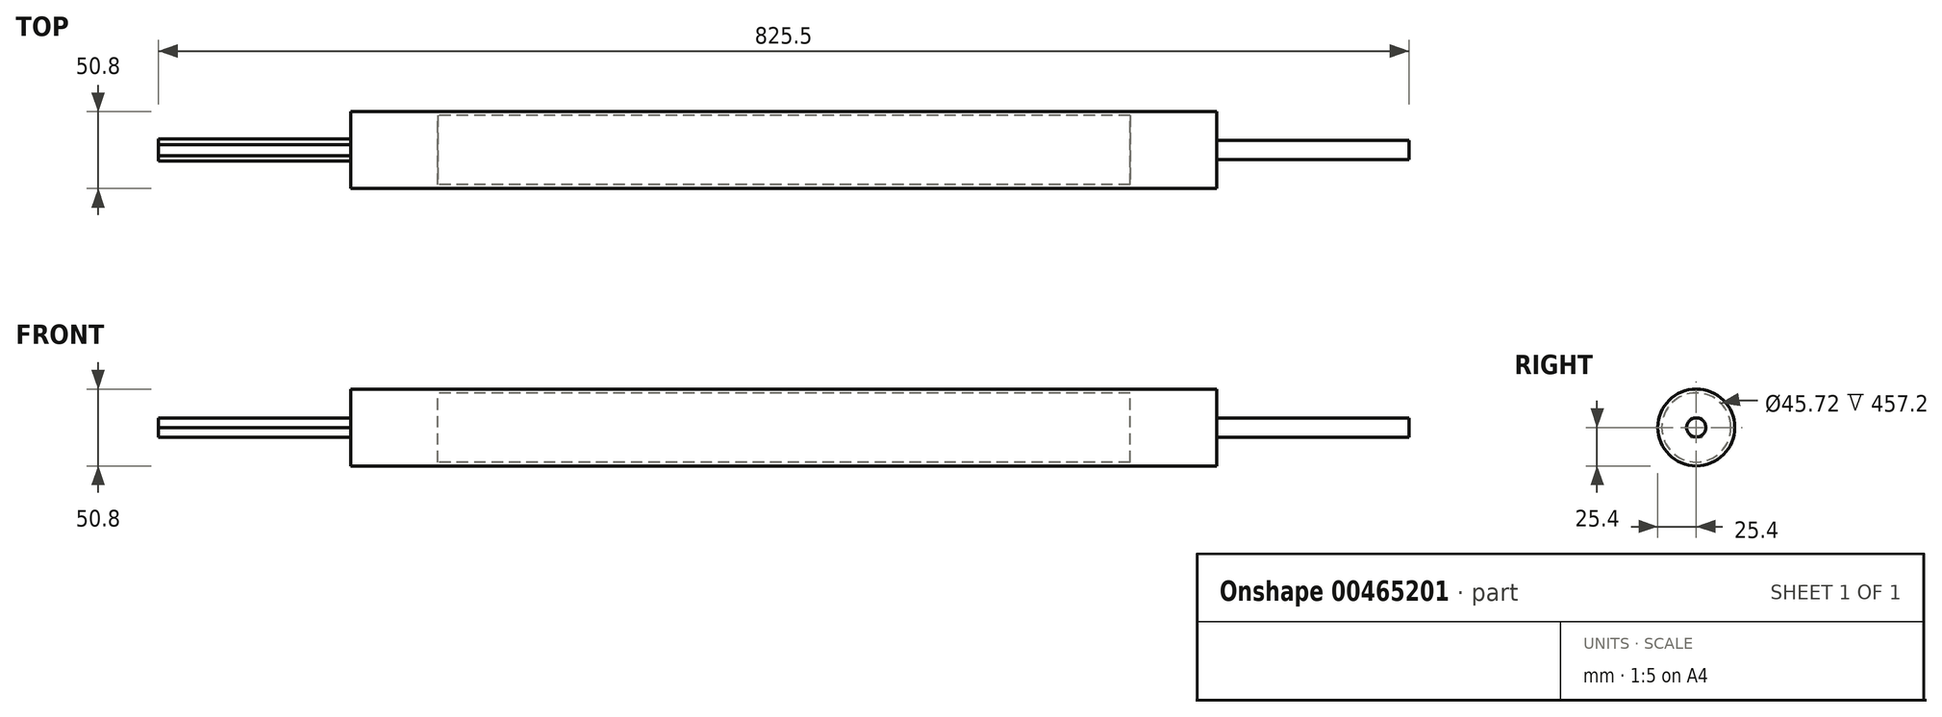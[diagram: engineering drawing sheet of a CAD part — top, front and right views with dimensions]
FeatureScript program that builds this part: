
annotation { "Feature Type Name" : "Feature", "Feature Type Description" : "" }
export const myFeature = defineFeature(function(context is Context, id is Id, definition is map)
    precondition{}
    {
        {
            var Q0;
            Q0=qCreatedBy(makeId("Right.planeOp"),FACE);
            var sketch = newSketch(context, id + "F0", { "sketchPlane" : qUnion([Q0])});
            skCircle(sketch, "E0", {"center": v(0, 0) * mm, "radius": 25.4 * mm});
            skCircle(sketch, "E1", {"center": v(0, 0) * mm, "radius": 22.86 * mm});
            skSolve(sketch);
        }
        {
            var Q0;
            Q0=makeQuery(id+"F0.imprint","IMPRINT",FACE,{"disambiguationData":[TD([[makeQuery(id+"F0.imprint","IMPRINT",EDGE,{"derivedFrom":sQuery(id+"F0.wireOp",EDGE,"E0")}),1.0]])]});
            extrude(context, id + "F1", {"entities" : qUnion([Q0]), "depth" : 558.8 * mm});
        }
        {
            var Q0;
            Q0=makeQuery(id+"F1.opExtrude","CAP_FACE",FACE,{"disambiguationData":[OSD([sQuery(id+"F0.wireOp",EDGE,"E0"),sQuery(id+"F0.wireOp",EDGE,"E1")])],"isStart":false});
            var sketch = newSketch(context, id + "F2", { "sketchPlane" : qUnion([Q0])});
            skCircle(sketch, "E2.0", {"center": v(0, 0) * mm, "radius": 22.86 * mm});
            skCircle(sketch, "E3", {"center": v(0, 0) * mm, "radius": 25.4 * mm});
            skCircle(sketch, "E4", {"center": v(0, 0) * mm, "radius": 6.35 * mm});
            skSolve(sketch);
        }
        {
            var Q0;
            Q0=makeQuery(id+"F2.imprint","IMPRINT",FACE,{"disambiguationData":[TD([[makeQuery(id+"F2.imprint","IMPRINT",EDGE,{"derivedFrom":sQuery(id+"F2.wireOp",EDGE,"E2.0")}),1.0]])]});
            var Q1;
            Q1=makeQuery(id+"F2.imprint","IMPRINT",FACE,{"disambiguationData":[TD([[makeQuery(id+"F2.imprint","IMPRINT",EDGE,{"derivedFrom":sQuery(id+"F2.wireOp",EDGE,"E4")}),1.0]])]});
            extrude(context, id + "F3", {"entities" : qUnion([Q0, Q1]), "oppositeDirection" : true, "depth" : 50.8 * mm});
        }
        {
            var Q0;
            Q0=makeQuery(id+"F2.imprint","IMPRINT",FACE,{"disambiguationData":[TD([[makeQuery(id+"F2.imprint","IMPRINT",EDGE,{"derivedFrom":sQuery(id+"F2.wireOp",EDGE,"E4")}),1.0]])]});
            extrude(context, id + "F4", {"entities" : qUnion([Q0]), "operationType" : NewBodyOperationType.ADD, "depth" : 133.35 * mm});
        }
        {
            var Q0;
            Q0=makeQuery(id+"F2.imprint","IMPRINT",FACE,{"disambiguationData":[TD([[makeQuery(id+"F2.imprint","IMPRINT",EDGE,{"derivedFrom":sQuery(id+"F2.wireOp",EDGE,"E2.0")}),1.0]])]});
            var Q1;
            Q1=makeQuery(id+"F2.imprint","IMPRINT",FACE,{"disambiguationData":[TD([[makeQuery(id+"F2.imprint","IMPRINT",EDGE,{"derivedFrom":sQuery(id+"F2.wireOp",EDGE,"E2.0")}),-1.0]])]});
            var Q2;
            Q2=makeQuery(id+"F2.imprint","IMPRINT",FACE,{"disambiguationData":[TD([[makeQuery(id+"F2.imprint","IMPRINT",EDGE,{"derivedFrom":sQuery(id+"F2.wireOp",EDGE,"E3")}),1.0]])]});
            var Q3;
            Q3=makeQuery(id+"F2.imprint","IMPRINT",FACE,{"disambiguationData":[TD([[makeQuery(id+"F2.imprint","IMPRINT",EDGE,{"derivedFrom":sQuery(id+"F2.wireOp",EDGE,"E4")}),1.0]])]});
            extrude(context, id + "F5", {"entities" : qUnion([Q0, Q1, Q2, Q3]), "operationType" : NewBodyOperationType.ADD, "depth" : 6.35 * mm});
        }
        {
            var Q0;
            Q0=makeQuery(id+"F1.opExtrude","CAP_FACE",FACE,{"disambiguationData":[OSD([sQuery(id+"F0.wireOp",EDGE,"E0"),sQuery(id+"F0.wireOp",EDGE,"E1")])],"isStart":true});
            var sketch = newSketch(context, id + "F6", { "sketchPlane" : qUnion([Q0])});
            skCircle(sketch, "E5", {"center": v(0, 0) * mm, "radius": 25.4 * mm});
            skCircle(sketch, "E6.0", {"center": v(0, 0) * mm, "radius": 22.86 * mm});
            skCircle(sketch, "E7.cCircle", {"center": v(0, 0) * mm, "radius": 6.35 * mm, "construction": true});
            skLineSegment(sketch, "E7.0", {"start": v(3.67, -6.35) * mm, "end": v(-3.67, -6.35) * mm});
            skLineSegment(sketch, "E7.1", {"start": v(-3.67, -6.35) * mm, "end": v(-7.33, 0) * mm});
            skLineSegment(sketch, "E7.2", {"start": v(-7.33, 0) * mm, "end": v(-3.67, 6.35) * mm});
            skLineSegment(sketch, "E7.3", {"start": v(-3.67, 6.35) * mm, "end": v(3.67, 6.35) * mm});
            skLineSegment(sketch, "E7.4", {"start": v(3.67, 6.35) * mm, "end": v(7.33, 0) * mm});
            skLineSegment(sketch, "E7.5", {"start": v(7.33, 0) * mm, "end": v(3.67, -6.35) * mm});
            skPoint(sketch, "E7.0.midPoint", {"position": v(0, -6.35) * mm});
            skSolve(sketch);
        }
        {
            var Q0;
            Q0=makeQuery(id+"F6.imprint","IMPRINT",FACE,{"disambiguationData":[TD([[makeQuery(id+"F6.imprint","IMPRINT",EDGE,{"derivedFrom":sQuery(id+"F6.wireOp",EDGE,"E6.0")}),-1.0]])]});
            var Q1;
            Q1=makeQuery(id+"F6.imprint","IMPRINT",FACE,{"disambiguationData":[TD([[makeQuery(id+"F6.imprint","IMPRINT",EDGE,{"derivedFrom":sQuery(id+"F6.wireOp",EDGE,"E7.0")}),-1.0]])]});
            extrude(context, id + "F7", {"entities" : qUnion([Q0, Q1]), "oppositeDirection" : true, "depth" : 50.8 * mm});
        }
        {
            var Q0;
            Q0=makeQuery(id+"F6.imprint","IMPRINT",FACE,{"disambiguationData":[TD([[makeQuery(id+"F6.imprint","IMPRINT",EDGE,{"derivedFrom":sQuery(id+"F6.wireOp",EDGE,"E7.0")}),-1.0]])]});
            extrude(context, id + "F8", {"entities" : qUnion([Q0]), "operationType" : NewBodyOperationType.ADD, "depth" : 133.35 * mm});
        }
        {
            var Q0;
            Q0 = qSketchRegion(id + "F6", true);
            var Q1;
            Q1=makeQuery(id+"F6.imprint","IMPRINT",FACE,{"disambiguationData":[TD([[makeQuery(id+"F6.imprint","IMPRINT",EDGE,{"derivedFrom":sQuery(id+"F6.wireOp",EDGE,"E6.0")}),-1.0]])]});
            extrude(context, id + "F9", {"entities" : qUnion([Q0, Q1]), "operationType" : NewBodyOperationType.ADD, "depth" : 6.35 * mm});
        }
    });
